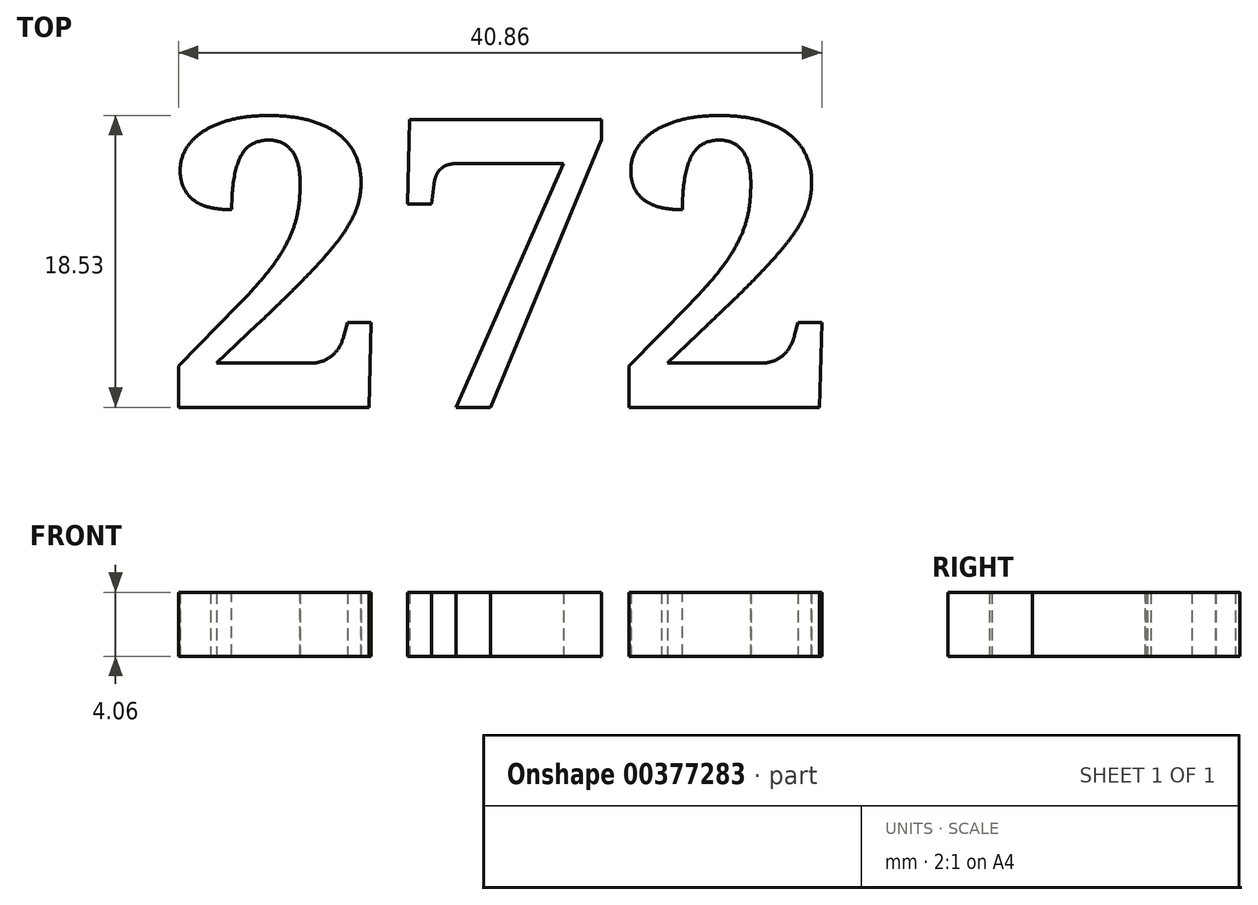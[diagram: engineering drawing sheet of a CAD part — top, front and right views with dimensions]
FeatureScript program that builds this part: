
annotation { "Feature Type Name" : "Feature", "Feature Type Description" : "" }
export const myFeature = defineFeature(function(context is Context, id is Id, definition is map)
    precondition{}
    {
        {
            var Q0;
            Q0=qCreatedBy(makeId("Top.planeOp"),FACE);
            var sketch = newSketch(context, id + "F0", { "sketchPlane" : qUnion([Q0])});
            skText(sketch, "E0", { "text": "272", "fontName": "NotoSerif-Bold.ttf"});
            const initialGuessF0  = {"E0": [0, 0, 1, 0, 0.01843]};
            skSetInitialGuess(sketch, initialGuessF0);
            skSolve(sketch);
        }
        {
            var Q0;
            Q0 = qSketchRegion(id + "F0", true);
            extrude(context, id + "F1", {"entities" : qUnion([Q0]), "depth" : 4.06 * mm});
        }
    });
